# Revit family: Remeha_Gas110Eco-65_LOD-3
name_source: partatom
category: Mechanical Equipment
revit_build: Autodesk Revit 2015 (Build: 20160512_1515(x64)
units: mm (PartAtom-declared; Revit-internal decimal feet)

## types (2) — shared parameters
6 Monthly = 0
Access Clearance Bottom = 0 mm
Access Clearance Front = 700 mm
Access Clearance Left = 25 mm
Access Clearance Rear = 0 mm
Access Clearance Right = 25 mm
Access Clearance Top = 400 mm
Additional Technical Details = https://www.remeha.co.uk
Air Inlet Connection Size = 150 mm
Annually = As per attached URL O&M manual
Assembly Code = D3020100
BMS Links = Yes
Bespoke Timeframe = 0
Building Regulations Seasonal Efficiency = 96.30 %
Burner Control Type = Modulating
CE Mark = CE - 0063BS3826
Colour = Remeha White + RAL 2002
Condensate Drain Size = 32 mm
Condensate Drain Type = Plain
Configuration = Single boiler
Control Type = 0 - 10V, Open Therm, Volt free enable, Direct boiler weather compensating control systems available from Remeha as optional extra's.
Daily = 0
Default Elevation = 0 mm
Description = Condensing Boiler
Drain Connection Size = 0 mm
Drain Connection Type = Unset
Embodied Carbon = 0
Energy Technology List = https://etl.beis.gov.uk
Environmental Product Declaration = 0
ErP Energy Label = A
ErP Rated Efficiency at Full Load = 88.6 %
ErP Rated Efficiency at Part Load = 98.1 %
ErP Seasonal Efficiency = 93 %
Expected Life = 15
External Material = Steel
Features = Remeha's Gas110 range are compact high efficiency floor standing condensing boilers have been developed specifically to fit directly into the floor space as a traditional boiler.
Finish = Painted
Flow and Return Connection Size = 32 mm
Flow and Return Connection Type = Threaded
Flue Connection size = 100 mm
Flue or Air Intake Classification = B23p,C13,C33,C43,C53,C63,C83,C93
Frequency = 50 Hz
Fuel Connection Size = 20 mm
Fuel Connection Type = Threaded
Full Load Current = 0 A
Fuse Rating = 6 A
Gas Consumption rate = 6.56 m3/h
Green Guide for Specification = 0
Gross Weight = 122.50 kg
Heat Exchanger Material = Aluminium
Heater Operation = Condensing
IK Rating = 0
IP Rating = IP21
IfcExportAs = IfcBoilerType
IfcExportType = NOTDEFINED
Interlocks = Yes
Life Cycle Analysis = 0
Location of Manufacturer = 0
Maintenance Required 0 to 300hrs = 0
Maintenance Required 1001 to 2000hrs = 0
Maintenance Required 2001 to 4000hrs = 0
Maintenance Required 301 to 600hrs = 0
Maintenance Required 4001 to 8000hrs = 0
Maintenance Required 601 to 1000hrs = 0
Maintenance Required 8001 to 12000hrs = 0
Manufacturer = Remeha Commercial
Manufacturer Website = http://www.remeha.co.uk
Material Ingredient Reporting = 0
Maximum Oil Inlet Pressure = 0.00 bar
Maximum Power Consumption = 88 W
Minimum Oil Inlet Pressure = 0.00 bar
Minimum Power Consumption = 31 W
Monthly = 0
Mounting = Floor Standing
NOx Emissions = 32 mg/kWh
Nominal Oil Inlet Pressure = 0.00 bar
Operation and Maintenance Manual = https://www.remeha.co.uk
Optional Fuel = Gas - LPG
Overall Height = 1100 mm
Overall Length = 663 mm
Overall Width = 600 mm
Primary Fuel = Gas - NG
Product Literature = https://www.remeha.co.uk
Product Model Number = 100010820
Product Range = Gas 110 Eco - 65
Quarterly = 0
Rated Criteria = 80/60
Rated Output = 61000 W
Reference Standard = 92/42/EEC, 2006/95/EEC, 2004/108/EEC, 97/23/EEC (article 3 sub 3)
Responsible Extraction of Materials = 0
Responsible Sourcing of Materials = 0
Safety Valve Connection Size = 0 mm
Safety Valve Connection Type = Unset
Shape = Rectangular (Vertical)
Shipping Weight = 116.00 kg
Sound Pressure Level = 49 dBA
Starting Current = 0 A
Supply Phase = 1
Turndown Ratio = 5:1
Type = Space heating
Type Image = <None>
Voltage = 230 V
Water Treatment Required = Yes
Weekly = 0
zero-valued in all types: Cost, Oil Consumption rate

## per-type parameters (varying)
| type | Hydraulic Resistance at 11C temperature differential | Hydraulic Resistance at 20C temperature differential | Keynote | Maximum Gas Inlet Pressure | Maximum Operating Pressure | Minimum Flow Rate at 11C temperature differential | Minimum Flow Rate at 20C temperature differential | Minimum Gas Inlet Pressure | Minimum Operating Pressure | Model | Nominal Gas Inlet Pressure | URL | Water Content |
| Gas 110 Eco-65 | 0.00 | 0.00 | Flue Connection size can vary between 100/150 concentric. | 0.00 bar | 0.01 bar | 0.083 L/s | 0.046 L/s | 0.00 bar | 0.00 bar | Gas 110 Eco - 65 | 0.00 bar | http://www.remeha.co.uk | 24.6 L |
| Gas 110 Eco - 65 | 0.58 | 0.18 |  | 0.03 bar | 4.00 bar | 1.320 L/s | 0.730 L/s | 0.02 bar | 0.80 bar | Gas 110 Eco - 115 | 0.02 bar |  | 6.5 L |

note: source unit labels omitted for Hydraulic Resistance at 11C temperature differential, Hydraulic Resistance at 20C temperature differential — the stored unit's dimension contradicts the parameter name (converter mislabeling)

## geometry (parser evidence)
native form markers: Blend x21, Sweep x13
no freeform markers — native parametric forms only
